# Revit family: 32L-C-P-ID
name_source: partatom
category: Lighting Fixtures
revit_build: Autodesk Revit 2014 (Build: 20130308_1515(x64)
units: mm (PartAtom-declared; Revit-internal decimal feet)

## types (1)
- 32L-C-P-ID
    Apparent Load = 0 VA
    Assembly Code = D5020210
    Color Filter = 16777215
    Default Elevation = 4' - 0"
    Description = Inde-Pendant 32 LED Cylinder Pendant Indirect/Direct
    Dimming Lamp Color Temperature Shift = <None>
    Emit Shape Visible in Rendering = No
    Emit from Circle Diameter = 0' - 6"
    Glass = Glass - Hubbell - White
    Lamp = LED
    Load Classification = Lighting
    Manufacturer = Lite Control
    Material = Hubbell - White
    Model = 32L-C-P-ID
    Pendant Height = 2' - 0"
    Photometric Link = https://www.hubbell.com
    Photometric Notes = More IES files downloaded in the Photometric Link
    Photometric Web File = 32L-C-P-ID-C1-AC1-30K-I265-D055.IES
    Power Factor = 1
    Product Documentation Link = https://hubbellcdn.com
    Product Page URL = https://www.hubbell.com
    Tilt Angle = 90.00°
    Type Comments = Lighting Fixtures
    URL = https://www.hubbell.com
    Voltage = 120 V
    Warranty = 5 years Warranty
    Watts = 7 W

## geometry (parser evidence)
native form markers: Blend x2, Sweep x2
no freeform markers — native parametric forms only
